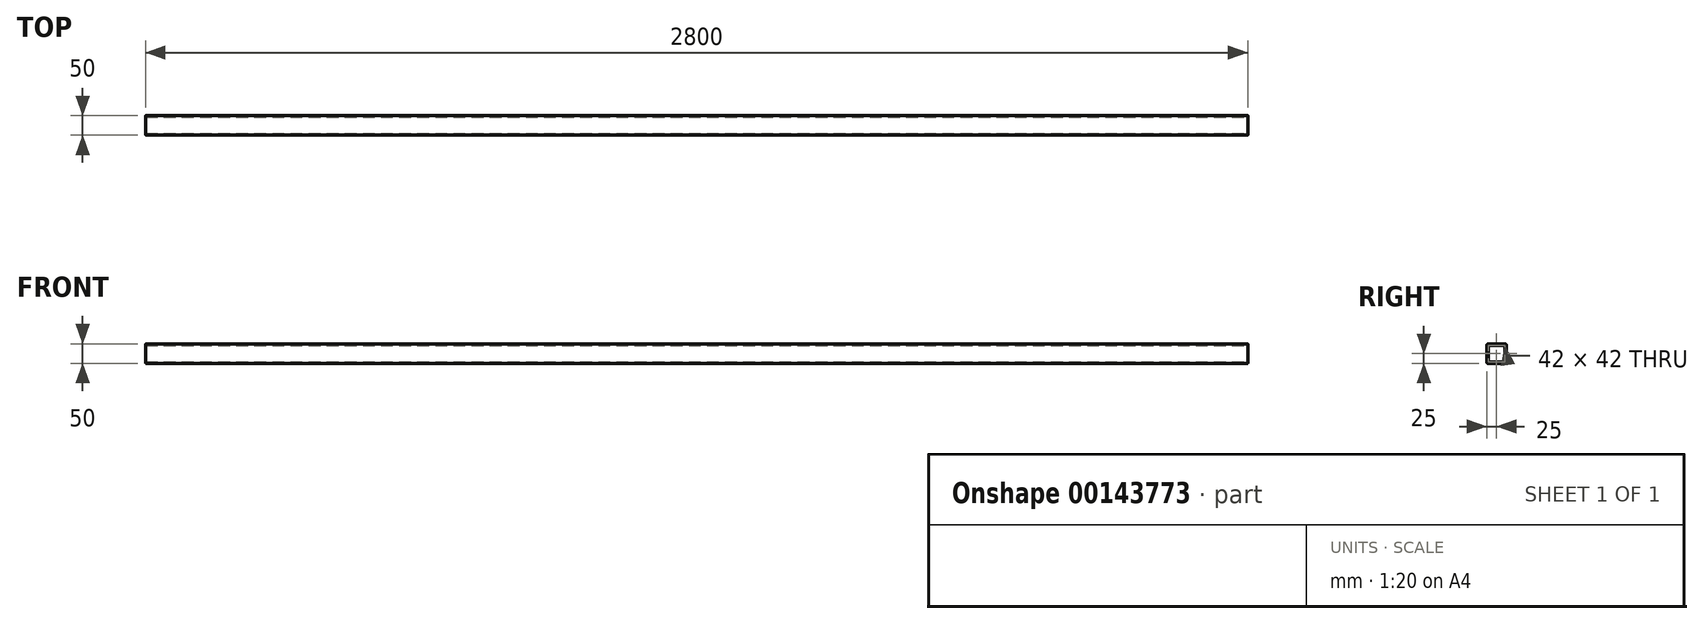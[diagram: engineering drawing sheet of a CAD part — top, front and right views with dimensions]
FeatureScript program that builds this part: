
annotation { "Feature Type Name" : "Feature", "Feature Type Description" : "" }
export const myFeature = defineFeature(function(context is Context, id is Id, definition is map)
    precondition{}
    {
        {
            var Q0;
            Q0=qCreatedBy(makeId("Right.planeOp"),FACE);
            var sketch = newSketch(context, id + "F0", { "sketchPlane" : qUnion([Q0])});
            skLineSegment(sketch, "E0.bottom", {"start": v(-21, 25) * mm, "end": v(21, 25) * mm});
            skLineSegment(sketch, "E0.top", {"start": v(-21, -25) * mm, "end": v(21, -25) * mm});
            skLineSegment(sketch, "E0.left", {"start": v(-25, 21) * mm, "end": v(-25, -21) * mm});
            skLineSegment(sketch, "E0.right", {"start": v(25, 21) * mm, "end": v(25, -21) * mm});
            skPoint(sketch, "E1.visualSharp", {"position": v(-25, 25) * mm});
            skArc(sketch, "E1.filletArc", {"start": v(-21, 25) * mm, "mid": v(-23.83, 23.83) * mm, "end": v(-25, 21) * mm});
            skPoint(sketch, "E2.visualSharp", {"position": v(-25, -25) * mm});
            skArc(sketch, "E2.filletArc", {"start": v(-25, -21) * mm, "mid": v(-23.83, -23.83) * mm, "end": v(-21, -25) * mm});
            skPoint(sketch, "E3.visualSharp", {"position": v(25, -25) * mm});
            skArc(sketch, "E3.filletArc", {"start": v(21, -25) * mm, "mid": v(23.83, -23.83) * mm, "end": v(25, -21) * mm});
            skPoint(sketch, "E4.visualSharp", {"position": v(25, 25) * mm});
            skArc(sketch, "E4.filletArc", {"start": v(25, 21) * mm, "mid": v(23.83, 23.83) * mm, "end": v(21, 25) * mm});
            skLineSegment(sketch, "E5.0", {"start": v(21, 21) * mm, "end": v(21, -21) * mm});
            skLineSegment(sketch, "E5.1", {"start": v(-21, 21) * mm, "end": v(21, 21) * mm});
            skLineSegment(sketch, "E5.2", {"start": v(-21, 21) * mm, "end": v(-21, -21) * mm});
            skLineSegment(sketch, "E5.3", {"start": v(-21, -21) * mm, "end": v(21, -21) * mm});
            skSolve(sketch);
        }
        {
            var Q0;
            Q0=makeQuery(id+"F0.imprint","IMPRINT",FACE,{"disambiguationData":[TD([[makeQuery(id+"F0.imprint","IMPRINT",EDGE,{"derivedFrom":sQuery(id+"F0.wireOp",EDGE,"E0.bottom")}),-1.0]])]});
            extrude(context, id + "F1", {"entities" : qUnion([Q0]), "endBound" : BoundingType.SYMMETRIC, "oppositeDirection" : true, "depth" : 2800 * mm});
        }
    });
